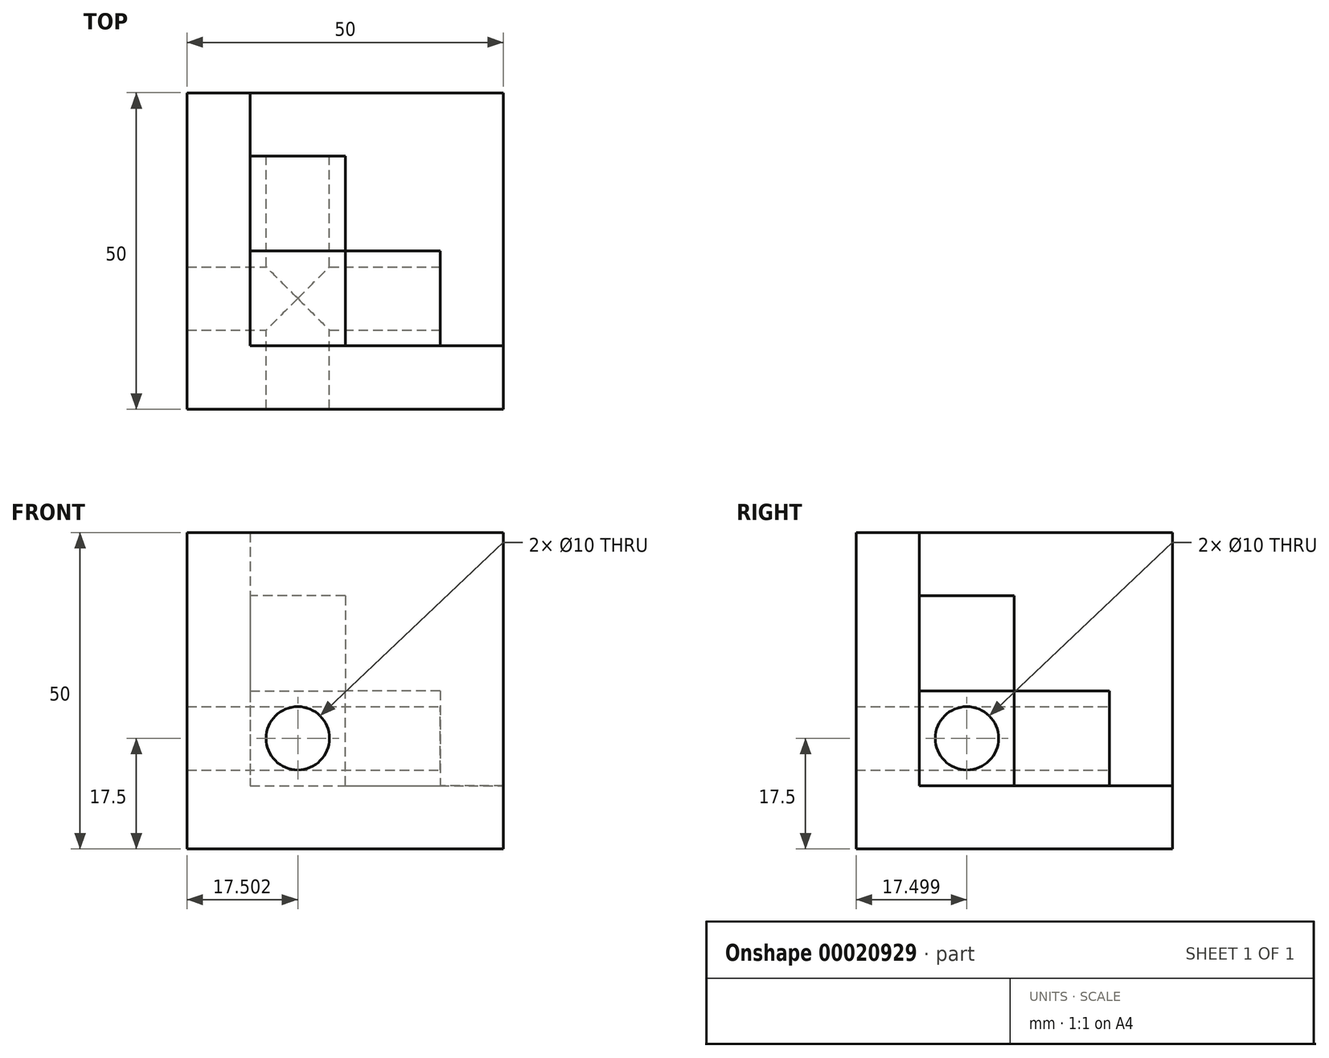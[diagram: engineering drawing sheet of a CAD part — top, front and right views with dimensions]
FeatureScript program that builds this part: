
annotation { "Feature Type Name" : "Feature", "Feature Type Description" : "" }
export const myFeature = defineFeature(function(context is Context, id is Id, definition is map)
    precondition{}
    {
        {
            var Q0;
            Q0=qCreatedBy(makeId("Top.planeOp"),FACE);
            var sketch = newSketch(context, id + "F0", { "sketchPlane" : qUnion([Q0])});
            skLineSegment(sketch, "E0.bottom", {"start": v(-36.68, -12.64) * mm, "end": v(13.32, -12.64) * mm});
            skLineSegment(sketch, "E0.top", {"start": v(-36.68, -62.64) * mm, "end": v(13.32, -62.64) * mm});
            skLineSegment(sketch, "E0.left", {"start": v(-36.68, -12.64) * mm, "end": v(-36.68, -62.64) * mm});
            skLineSegment(sketch, "E0.right", {"start": v(13.32, -12.64) * mm, "end": v(13.32, -62.64) * mm});
            skSolve(sketch);
        }
        {
            var Q0;
            Q0=makeQuery(id+"F0.imprint","IMPRINT",FACE,{"disambiguationData":[TD([[makeQuery(id+"F0.imprint","IMPRINT",EDGE,{"derivedFrom":sQuery(id+"F0.wireOp",EDGE,"E0.bottom")}),-1.0]])]});
            extrude(context, id + "F1", {"entities" : qUnion([Q0]), "depth" : 10 * mm});
        }
        {
            var Q0;
            Q0=makeQuery(id+"F1.opExtrude","CAP_FACE",FACE,{"disambiguationData":[OSD([sQuery(id+"F0.wireOp",EDGE,"E0.bottom"),sQuery(id+"F0.wireOp",EDGE,"E0.top"),sQuery(id+"F0.wireOp",EDGE,"E0.left"),sQuery(id+"F0.wireOp",EDGE,"E0.right")])],"isStart":false});
            var sketch = newSketch(context, id + "F2", { "sketchPlane" : qUnion([Q0])});
            skLineSegment(sketch, "E1.bottom", {"start": v(13.32, -12.64) * mm, "end": v(-26.68, -12.64) * mm});
            skLineSegment(sketch, "E1.top", {"start": v(13.32, -52.64) * mm, "end": v(-26.68, -52.64) * mm});
            skLineSegment(sketch, "E1.left", {"start": v(13.32, -12.64) * mm, "end": v(13.32, -52.64) * mm});
            skLineSegment(sketch, "E1.right", {"start": v(-26.68, -12.64) * mm, "end": v(-26.68, -52.64) * mm});
            skSolve(sketch);
        }
        {
            var Q0;
            {var subQ1=sQuery(id+"F2.wireOp",EDGE,"E1.top");Q0=makeQuery(id+"F2.imprint","IMPRINT",FACE,{"disambiguationData":[TD([[makeQuery(id+"F2.imprint","IMPRINT",EDGE,{"derivedFrom":subQ1}),1.0]])]});}
            extrude(context, id + "F3", {"entities" : qUnion([Q0]), "operationType" : NewBodyOperationType.ADD, "depth" : 40 * mm});
        }
        {
            var Q0;
            Q0=makeQuery(id+"F1.opExtrude","CAP_FACE",FACE,{"disambiguationData":[OSD([sQuery(id+"F0.wireOp",EDGE,"E0.bottom"),sQuery(id+"F0.wireOp",EDGE,"E0.top"),sQuery(id+"F0.wireOp",EDGE,"E0.left"),sQuery(id+"F0.wireOp",EDGE,"E0.right")])],"isStart":false});
            var sketch = newSketch(context, id + "F4", { "sketchPlane" : qUnion([Q0])});
            skLineSegment(sketch, "E2.bottom", {"start": v(-26.68, -52.64) * mm, "end": v(-11.68, -52.64) * mm});
            skLineSegment(sketch, "E2.top", {"start": v(-26.68, -37.64) * mm, "end": v(-11.68, -37.64) * mm});
            skLineSegment(sketch, "E2.left", {"start": v(-26.68, -52.64) * mm, "end": v(-26.68, -37.64) * mm});
            skLineSegment(sketch, "E2.right", {"start": v(-11.68, -52.64) * mm, "end": v(-11.68, -37.64) * mm});
            skSolve(sketch);
        }
        {
            var Q0;
            Q0=makeQuery(id+"F4.imprint","IMPRINT",FACE,{"disambiguationData":[TD([[makeQuery(id+"F4.imprint","IMPRINT",EDGE,{"derivedFrom":sQuery(id+"F4.wireOp",EDGE,"E2.bottom")}),-1.0]])]});
            extrude(context, id + "F5", {"entities" : qUnion([Q0]), "operationType" : NewBodyOperationType.ADD, "depth" : 30 * mm});
        }
        {
            var Q0;
            Q0=makeQuery(id+"F5.opExtrude","SWEPT_FACE",FACE,{"disambiguationData":[OSD([sQuery(id+"F4.wireOp",EDGE,"E2.right")])]});
            var sketch = newSketch(context, id + "F6", { "sketchPlane" : qUnion([Q0])});
            skLineSegment(sketch, "E3.bottom", {"start": v(-52.64, 10) * mm, "end": v(-37.64, 10) * mm});
            skLineSegment(sketch, "E3.top", {"start": v(-52.64, 25) * mm, "end": v(-37.64, 25) * mm});
            skLineSegment(sketch, "E3.left", {"start": v(-52.64, 10) * mm, "end": v(-52.64, 25) * mm});
            skLineSegment(sketch, "E3.right", {"start": v(-37.64, 10) * mm, "end": v(-37.64, 25) * mm});
            skSolve(sketch);
        }
        {
            var Q0;
            Q0=makeQuery(id+"F6.imprint","IMPRINT",FACE,{"disambiguationData":[TD([[makeQuery(id+"F6.imprint","IMPRINT",EDGE,{"derivedFrom":sQuery(id+"F6.wireOp",EDGE,"E3.bottom")}),1.0]])]});
            extrude(context, id + "F7", {"entities" : qUnion([Q0]), "operationType" : NewBodyOperationType.ADD, "depth" : 15 * mm});
        }
        {
            var Q0;
            Q0=makeQuery(id+"F7.boolean.opBoolean","MERGE",FACE,{"derivedFrom":[makeQuery(id+"F5.opExtrude","SWEPT_FACE",FACE,{"disambiguationData":[OSD([sQuery(id+"F4.wireOp",EDGE,"E2.top")])]}),makeQuery(id+"F7.opExtrude","SWEPT_FACE",FACE,{"disambiguationData":[OSD([sQuery(id+"F6.wireOp",EDGE,"E3.right")])]})]});
            var sketch = newSketch(context, id + "F8", { "sketchPlane" : qUnion([Q0])});
            skLineSegment(sketch, "E4.bottom", {"start": v(26.68, 10) * mm, "end": v(11.68, 10) * mm});
            skLineSegment(sketch, "E4.top", {"start": v(26.68, 25) * mm, "end": v(11.68, 25) * mm});
            skLineSegment(sketch, "E4.left", {"start": v(26.68, 10) * mm, "end": v(26.68, 25) * mm});
            skLineSegment(sketch, "E4.right", {"start": v(11.68, 10) * mm, "end": v(11.68, 25) * mm});
            skSolve(sketch);
        }
        {
            var Q0;
            Q0=makeQuery(id+"F8.imprint","IMPRINT",FACE,{"disambiguationData":[TD([[makeQuery(id+"F8.imprint","IMPRINT",EDGE,{"derivedFrom":sQuery(id+"F8.wireOp",EDGE,"E4.bottom")}),-1.0]])]});
            extrude(context, id + "F9", {"entities" : qUnion([Q0]), "operationType" : NewBodyOperationType.ADD, "depth" : 15 * mm});
        }
        {
            var Q0;
            Q0=makeQuery(id+"F7.opExtrude","CAP_FACE",FACE,{"disambiguationData":[OSD([sQuery(id+"F6.wireOp",EDGE,"E3.bottom"),sQuery(id+"F6.wireOp",EDGE,"E3.top"),sQuery(id+"F6.wireOp",EDGE,"E3.left"),sQuery(id+"F6.wireOp",EDGE,"E3.right")])],"isStart":false});
            var sketch = newSketch(context, id + "F10", { "sketchPlane" : qUnion([Q0])});
            skCircle(sketch, "E5", {"center": v(-45.14, 17.5) * mm, "radius": 5 * mm});
            skSolve(sketch);
        }
        {
            var Q0;
            Q0=makeQuery(id+"F10.imprint","IMPRINT",FACE,{"disambiguationData":[TD([[makeQuery(id+"F10.imprint","IMPRINT",EDGE,{"derivedFrom":sQuery(id+"F10.wireOp",EDGE,"E5")}),1.0]])]});
            extrude(context, id + "F11", {"entities" : qUnion([Q0]), "operationType" : NewBodyOperationType.REMOVE, "oppositeDirection" : true, "depth" : 500 * mm});
        }
        {
            var Q0;
            Q0=makeQuery(id+"F9.opExtrude","CAP_FACE",FACE,{"disambiguationData":[OSD([sQuery(id+"F8.wireOp",EDGE,"E4.bottom"),sQuery(id+"F8.wireOp",EDGE,"E4.top"),sQuery(id+"F8.wireOp",EDGE,"E4.left"),sQuery(id+"F8.wireOp",EDGE,"E4.right")])],"isStart":false});
            var sketch = newSketch(context, id + "F12", { "sketchPlane" : qUnion([Q0])});
            skCircle(sketch, "E6", {"center": v(19.18, 17.5) * mm, "radius": 5 * mm});
            skSolve(sketch);
        }
        {
            var Q0;
            Q0=makeQuery(id+"F12.imprint","IMPRINT",FACE,{"disambiguationData":[TD([[makeQuery(id+"F12.imprint","IMPRINT",EDGE,{"derivedFrom":sQuery(id+"F12.wireOp",EDGE,"E6")}),1.0]])]});
            extrude(context, id + "F13", {"entities" : qUnion([Q0]), "operationType" : NewBodyOperationType.REMOVE, "oppositeDirection" : true, "depth" : 500 * mm});
        }
    });
